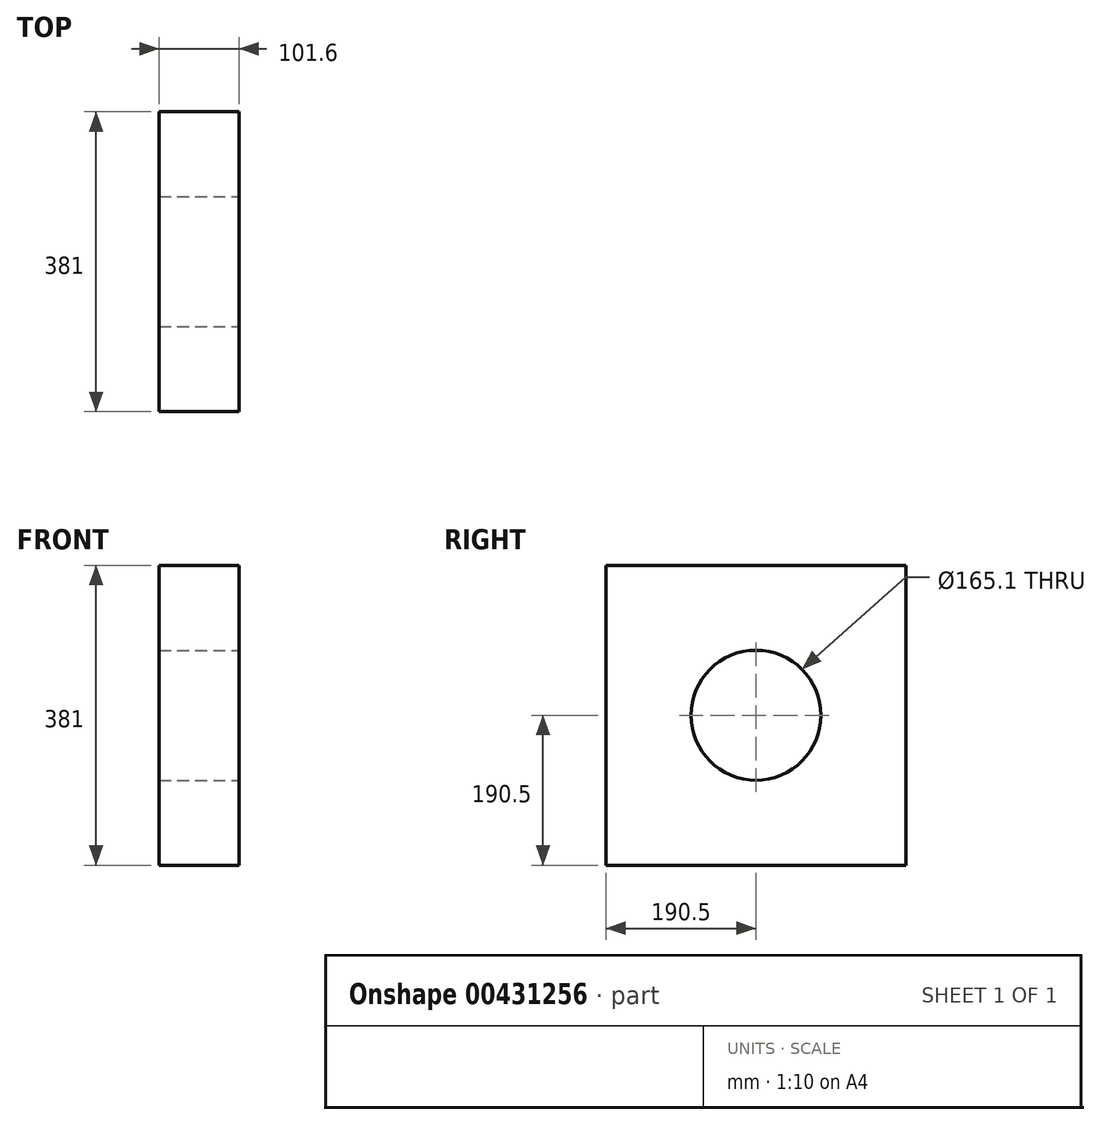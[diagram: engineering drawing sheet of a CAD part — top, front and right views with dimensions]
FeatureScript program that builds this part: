
annotation { "Feature Type Name" : "Feature", "Feature Type Description" : "" }
export const myFeature = defineFeature(function(context is Context, id is Id, definition is map)
    precondition{}
    {
        {
            var Q0;
            Q0=qCreatedBy(makeId("Right.planeOp"),FACE);
            var sketch = newSketch(context, id + "F0", { "sketchPlane" : qUnion([Q0])});
            skLineSegment(sketch, "E0.bottom", {"start": v(0, 0) * mm, "end": v(381, 0) * mm});
            skLineSegment(sketch, "E0.top", {"start": v(0, -381) * mm, "end": v(381, -381) * mm});
            skLineSegment(sketch, "E0.left", {"start": v(0, 0) * mm, "end": v(0, -381) * mm});
            skLineSegment(sketch, "E0.right", {"start": v(381, 0) * mm, "end": v(381, -381) * mm});
            skCircle(sketch, "E1", {"center": v(190.5, -190.5) * mm, "radius": 82.55 * mm});
            skPoint(sketch, "E2.trimOffspring.end.orphan", {"position": v(190.5, 0) * mm});
            skPoint(sketch, "E3.trimOffspring.end.orphan", {"position": v(381, -190.5) * mm});
            skPoint(sketch, "E4.start.orphan", {"position": v(190.5, -381) * mm});
            skPoint(sketch, "E5.start.orphan", {"position": v(0, -190.5) * mm});
            skSolve(sketch);
        }
        {
            var Q0;
            Q0=makeQuery(id+"F0.imprint","IMPRINT",FACE,{"disambiguationData":[TD([[makeQuery(id+"F0.imprint","IMPRINT",EDGE,{"derivedFrom":sQuery(id+"F0.wireOp",EDGE,"E0.bottom")}),-1.0]])]});
            extrude(context, id + "F1", {"entities" : qUnion([Q0]), "endBound" : BoundingType.SYMMETRIC, "oppositeDirection" : true, "offsetDistance" : 25.4 * mm, "depth" : 101.6 * mm});
        }
    });
